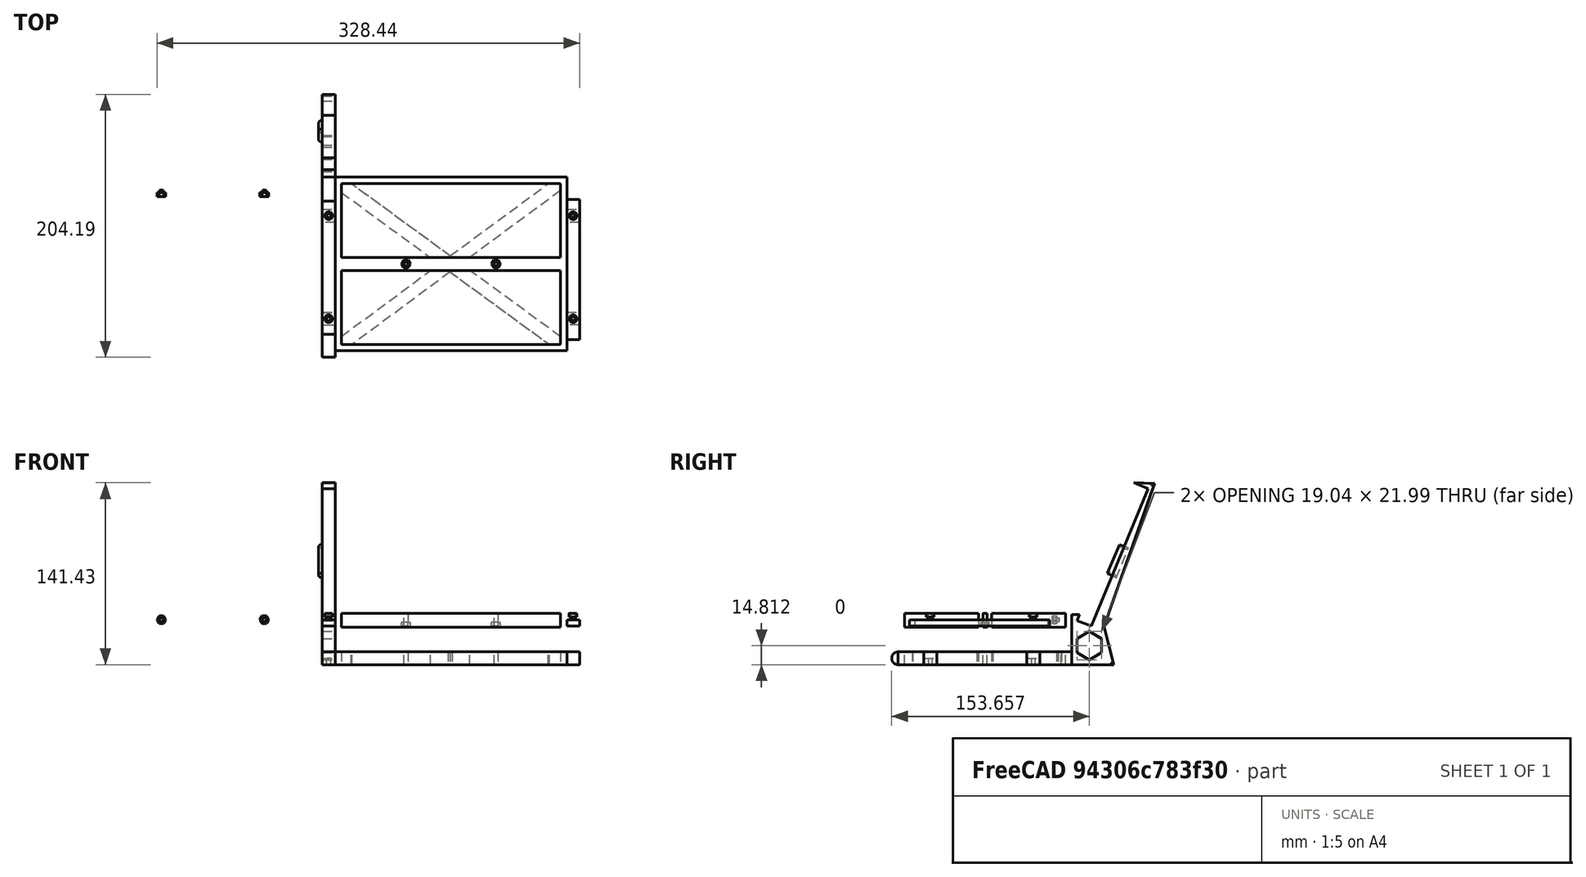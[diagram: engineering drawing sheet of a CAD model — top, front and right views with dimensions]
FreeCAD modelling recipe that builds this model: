
FCSTD DOCUMENT  (FreeCAD 0.16R6704 (Git))
Label: SOPORTE_BASE
License: All rights reserved
LicenseURL: http://en.wikipedia.org/wiki/All_rights_reserved
objects: Sketcher::SketchObject×13, PartDesign::Pocket×8, PartDesign::Pad×5, PartDesign::Fillet×3, Mesh::Feature×2
note: 42 computed .brp shape members not serialized (recipe doc carries the construction recipe); baked Part::Feature solids carry a one-line shape summary decoded from their .brp

FEATURE [Mesh::Feature] surround
  Placement = pos=(0,0,0) rot=(1,0,0;1.18682rad)
FEATURE [Sketcher::SketchObject] Sketch
  Placement = pos=(0,0,0) rot=(0.57735,0.57735,0.57735;2.0944rad)
  sketch-geometry (27):
    g0: LineSegment StartX=33.0856 StartY=111.432 StartZ=0 EndX=44.2008 EndY=106.79 EndZ=0
    g1: LineSegment StartX=44.2008 StartY=106.79 StartZ=0 EndX=0 EndY=0 EndZ=0
    g2: LineSegment StartX=-15 StartY=-20 StartZ=0 EndX=-40 EndY=-20 EndZ=0
    g3: LineSegment StartX=-150 StartY=-30 StartZ=0 EndX=17.4847 EndY=-30 EndZ=0
    g4: LineSegment StartX=17.4847 StartY=-30 StartZ=0 EndX=10 EndY=-0.272781 EndZ=0
    g5: LineSegment StartX=10 StartY=-0.272781 StartZ=0 EndX=49.1867 EndY=110.744 EndZ=0
    g6: LineSegment StartX=49.1867 StartY=110.744 StartZ=0 EndX=33.0856 EndY=111.432 EndZ=0
    g7: LineSegment StartX=0 StartY=0 StartZ=0 EndX=-10.9261 EndY=4.19036 EndZ=0
    g8: LineSegment StartX=-10.9261 StartY=4.19036 StartZ=0 EndX=-9.04306 EndY=8.84724 EndZ=0
    g9: LineSegment StartX=-9.04306 StartY=8.84724 StartZ=0 EndX=-15 EndY=8.84724 EndZ=0
    g10: LineSegment StartX=-15 StartY=8.84724 StartZ=0 EndX=-15 EndY=-20 EndZ=0
    g11: LineSegment StartX=8.17828 StartY=-20.6848 StartZ=0 EndX=8.17828 EndY=-9.6906 EndZ=0
    g12: LineSegment StartX=8.17828 StartY=-9.6906 StartZ=0 EndX=-1.34293 EndY=-4.19353 EndZ=0
    g13: LineSegment StartX=-1.34293 StartY=-4.19353 StartZ=0 EndX=-10.8641 EndY=-9.6906 EndZ=0
    g14: LineSegment StartX=-10.8641 StartY=-9.6906 StartZ=0 EndX=-10.8641 EndY=-20.6848 EndZ=0
    g15: LineSegment StartX=-10.8641 StartY=-20.6848 StartZ=0 EndX=-1.34293 EndY=-26.1818 EndZ=0
    g16: LineSegment StartX=-1.34293 StartY=-26.1818 StartZ=0 EndX=8.17828 EndY=-20.6848 EndZ=0
    g17: Circle [constr] CenterX=-1.34293 CenterY=-15.1877 CenterZ=0 NormalX=0 NormalY=0 NormalZ=1 Radius=10.9941
    g18: LineSegment StartX=-130 StartY=-20 StartZ=0 EndX=-130 EndY=-25 EndZ=0
    g19: LineSegment StartX=-130 StartY=-25 StartZ=0 EndX=-120 EndY=-25 EndZ=0
    g20: LineSegment StartX=-120 StartY=-25 StartZ=0 EndX=-120 EndY=-20 EndZ=0
    g21: LineSegment StartX=-130 StartY=-20 StartZ=0 EndX=-150 EndY=-20 EndZ=0
    g22: LineSegment StartX=-50 StartY=-20 StartZ=0 EndX=-50 EndY=-25 EndZ=0
    g23: LineSegment StartX=-50 StartY=-25 StartZ=0 EndX=-40 EndY=-25 EndZ=0
    g24: LineSegment StartX=-40 StartY=-25 StartZ=0 EndX=-40 EndY=-20 EndZ=0
    g25: LineSegment StartX=-50 StartY=-20 StartZ=0 EndX=-120 EndY=-20 EndZ=0
    g26: ArcOfCircle CenterX=-150 CenterY=-25 CenterZ=0 NormalX=0 NormalY=0 NormalZ=1 Radius=5 StartAngle=1.5708 EndAngle=4.71239
  constraints (57):
    c: Coincident(g0,g1)
    c: Coincident(g1,g-1)
    c: Horizontal(g2)
    c: Coincident(g3,g4)
    c: Coincident(g4,g5)
    c: Coincident(g5,g6)
    c: Coincident(g6,g0)
    c: Horizontal(g3)
    c: Coincident(g7,g8)
    c: Coincident(g8,g9)
    c: Coincident(g9,g10)
    c: Coincident(g-1,g7)
    c: Horizontal(g9)
    c: Coincident(g2,g10)
    c: DistanceY(g2,g-1) = 20
    c: DistanceY(g3,g-1) = 30
    c: DistanceX(g-1,g4) = 10
    c: Vertical(g10)
    c: DistanceX(g21,g2) = 135
    c: Coincident(g11,g12)
    c: Coincident(g12,g13)
    c: Coincident(g13,g14)
    c: Coincident(g14,g15)
    c: Coincident(g15,g16)
    c: Coincident(g16,g11)
    c: Equal(g11, g12-g16) x5
    c: PointOnObject(g11,g17)
    c: PointOnObject(g12,g17)
    c: PointOnObject(g13,g17)
    c: PointOnObject(g14,g17)
    c: PointOnObject(g15,g17)
    c: PointOnObject(g16,g17)
    c: Vertical(g14)
    c: DistanceX(g21,g-1) = 150
    c: Coincident(g18,g19)
    c: Horizontal(g19)
    c: Coincident(g19,g20)
    c: Vertical(g20)
    c: Vertical(g18)
    c: DistanceX(g19,g19) = 10
    c: Coincident(g25,g20)
    c: Coincident(g21,g18)
    c: Tangent(g2,g21)
    c: Coincident(g22,g23)
    c: Horizontal(g23)
    c: Coincident(g23,g24)
    c: Vertical(g24)
    c: Vertical(g22)
    c: DistanceX(g23,g23) = 10
    c: DistanceX(g19,g22) = 70
    c: Coincident(g2,g24)
    c: Coincident(g25,g22)
    c: Tangent(g2,g25)
    c: DistanceY(g24,g24) = 5
    c: DistanceY(g20,g20) = 5
    c: Tangent(g26,g21)
    c: Tangent(g3,g26)
FEATURE [PartDesign::Pad] Pad
  Length = 10
  Length2 = 100
  Placement = pos=(0,0,0) rot=(0.57735,0.57735,0.57735;2.0944rad)
  Sketch = -> Sketch
  Type = 0
FEATURE [Sketcher::SketchObject] Sketch001
  ExternalGeometry = -> [Pad]
  Placement = pos=(0,0,-25) rot=(0,0,-1;1.5708rad)
  Support = -> Pad [Face15]
  sketch-geometry (2):
    g0: Circle CenterX=45 CenterY=5 CenterZ=0 NormalX=0 NormalY=0 NormalZ=1 Radius=1.5
    g1: Circle CenterX=125 CenterY=5 CenterZ=0 NormalX=0 NormalY=0 NormalZ=1 Radius=1.5
  constraints (6):
    c: Radius(g0) = 1.5
    c: DistanceY(g-3,g0) = 5
    c: DistanceX(g-3,g0) = 5
    c: Radius(g1) = 1.5
    c: DistanceX(g1,g-4) = 5
    c: DistanceY(g-4,g1) = 5
FEATURE [PartDesign::Pocket] Pocket
  Length = 5
  Placement = pos=(0,0,0) rot=(0.57735,0.57735,0.57735;2.0944rad)
  Sketch = -> Sketch001
  Type = 0
FEATURE [Sketcher::SketchObject] Sketch003
  ExternalGeometry = -> [Pocket]
  Placement = pos=(0,0,0) rot=(0.57735,0.57735,-0.57735;4.18879rad)
  Support = -> Pocket [Face4]
  sketch-geometry (4):
    g0: LineSegment StartX=19.5719 StartY=-37.6948 StartZ=0 EndX=28.8724 EndY=-60.696 EndZ=0
    g1: LineSegment StartX=28.8724 StartY=-60.696 StartZ=0 EndX=22.072 EndY=-63.3961 EndZ=0
    g2: LineSegment StartX=22.072 StartY=-63.3961 StartZ=0 EndX=12.4716 EndY=-40.895 EndZ=0
    g3: LineSegment StartX=12.4716 StartY=-40.895 StartZ=0 EndX=19.5719 EndY=-37.6948 EndZ=0
  constraints (4):
    c: Coincident(g0,g1)
    c: Coincident(g1,g2)
    c: Coincident(g2,g3)
    c: Coincident(g3,g0)
FEATURE [PartDesign::Pad] Pad001
  Length = 3
  Length2 = 100
  Placement = pos=(0,0,0) rot=(0.57735,0.57735,0.57735;2.0944rad)
  Sketch = -> Sketch003
  Type = 0
FEATURE [PartDesign::Fillet] Fillet
  Base = -> Pad001 [Edge77,Edge73,Edge100,Edge80]
  Placement = pos=(0,0,0) rot=(0.57735,0.57735,0.57735;2.0944rad)
  Radius = 2
FEATURE [PartDesign::Fillet] Fillet001
  Base = -> Fillet [Edge62]
  Placement = pos=(0,0,0) rot=(0.57735,0.57735,0.57735;2.0944rad)
  Radius = 3
FEATURE [PartDesign::Fillet] Fillet002
  Base = -> Fillet001 [Edge37]
  Placement = pos=(0,0,0) rot=(0.57735,0.57735,0.57735;2.0944rad)
  Radius = 3
FEATURE [Sketcher::SketchObject] Sketch002
  Placement = pos=(0,0,-30) rot=(0.707107,0.707107,0;3.14159rad)
  Support = -> Fillet002 [Face5]
  sketch-geometry (14):
    g0: LineSegment StartX=-123.239 StartY=1.96418 StartZ=0 EndX=-121.507 EndY=4.96418 EndZ=0
    g1: LineSegment StartX=-121.507 StartY=4.96418 StartZ=0 EndX=-123.239 EndY=7.96418 EndZ=0
    g2: LineSegment StartX=-123.239 StartY=7.96418 StartZ=0 EndX=-126.704 EndY=7.96418 EndZ=0
    g3: LineSegment StartX=-126.704 StartY=7.96418 StartZ=0 EndX=-128.436 EndY=4.96418 EndZ=0
    g4: LineSegment StartX=-128.436 StartY=4.96418 StartZ=0 EndX=-126.704 EndY=1.96418 EndZ=0
    g5: LineSegment StartX=-126.704 StartY=1.96418 StartZ=0 EndX=-123.239 EndY=1.96418 EndZ=0
    g6: Circle [constr] CenterX=-124.971 CenterY=4.96418 CenterZ=0 NormalX=0 NormalY=0 NormalZ=1 Radius=3.4641
    g7: LineSegment StartX=-43.3346 StartY=7.98064 StartZ=0 EndX=-46.7987 EndY=7.98064 EndZ=0
    g8: LineSegment StartX=-46.7987 StartY=7.98064 StartZ=0 EndX=-48.5308 EndY=4.98064 EndZ=0
    g9: LineSegment StartX=-48.5308 StartY=4.98064 StartZ=0 EndX=-46.7987 EndY=1.98064 EndZ=0
    g10: LineSegment StartX=-46.7987 StartY=1.98064 StartZ=0 EndX=-43.3346 EndY=1.98064 EndZ=0
    g11: LineSegment StartX=-43.3346 StartY=1.98064 StartZ=0 EndX=-41.6026 EndY=4.98064 EndZ=0
    g12: LineSegment StartX=-41.6026 StartY=4.98064 StartZ=0 EndX=-43.3346 EndY=7.98064 EndZ=0
    g13: Circle [constr] CenterX=-45.0667 CenterY=4.98064 CenterZ=0 NormalX=0 NormalY=0 NormalZ=1 Radius=3.4641
  constraints (30):
    c: Coincident(g0,g1)
    c: Coincident(g1,g2)
    c: Coincident(g2,g3)
    c: Coincident(g3,g4)
    c: Coincident(g4,g5)
    c: Coincident(g5,g0)
    c: Equal(g0, g1-g5) x5
    c: PointOnObject(g0,g6)
    c: PointOnObject(g1,g6)
    c: PointOnObject(g2,g6)
    c: PointOnObject(g3,g6)
    c: PointOnObject(g4,g6)
    c: PointOnObject(g5,g6)
    c: Horizontal(g2)
    c: DistanceY(g0,g1) = 6
    c: Coincident(g7,g8)
    c: Coincident(g8,g9)
    c: Coincident(g9,g10)
    c: Coincident(g10,g11)
    c: Coincident(g11,g12)
    c: Coincident(g12,g7)
    c: Equal(g7, g8-g12) x5
    c: PointOnObject(g7,g13)
    c: PointOnObject(g8,g13)
    c: PointOnObject(g9,g13)
    c: PointOnObject(g10,g13)
    c: PointOnObject(g11,g13)
    c: PointOnObject(g12,g13)
    c: Horizontal(g7)
    c: DistanceY(g10,g7) = 6
FEATURE [PartDesign::Pocket] Pocket001
  Length = 3
  Placement = pos=(0,0,0) rot=(0.57735,0.57735,0.57735;2.0944rad)
  Sketch = -> Sketch002
  Type = 0
FEATURE [Mesh::Feature] SOPORTE_LATERAL_LADO
  Placement = pos=(192,0,0) rot=(0,0,1;0rad)
FEATURE [Sketcher::SketchObject] Sketch004
  Placement = pos=(0,0,-30) rot=(0,0,1;0rad)
  sketch-geometry (20):
    g0: LineSegment StartX=10 StartY=-50 StartZ=0 EndX=0 EndY=-50 EndZ=0
    g1: LineSegment StartX=0 StartY=-50 StartZ=0 EndX=0 EndY=-40 EndZ=0
    g2: LineSegment StartX=0 StartY=-40 StartZ=0 EndX=10 EndY=-40 EndZ=0
    g3: LineSegment StartX=10 StartY=-40 StartZ=0 EndX=10 EndY=-15 EndZ=0
    g4: LineSegment StartX=10 StartY=-15 StartZ=0 EndX=190 EndY=-15 EndZ=0
    g5: LineSegment StartX=190 StartY=-15 StartZ=0 EndX=190 EndY=-40 EndZ=0
    g6: LineSegment StartX=190 StartY=-40 StartZ=0 EndX=200 EndY=-40 EndZ=0
    g7: LineSegment StartX=200 StartY=-40 StartZ=0 EndX=200 EndY=-50 EndZ=0
    g8: LineSegment StartX=200 StartY=-50 StartZ=0 EndX=190 EndY=-50 EndZ=0
    g9: LineSegment StartX=190 StartY=-50 StartZ=0 EndX=190 EndY=-120 EndZ=0
    g10: LineSegment StartX=190 StartY=-120 StartZ=0 EndX=200 EndY=-120 EndZ=0
    g11: LineSegment StartX=200 StartY=-120 StartZ=0 EndX=200 EndY=-130 EndZ=0
    g12: LineSegment StartX=200 StartY=-130 StartZ=0 EndX=190 EndY=-130 EndZ=0
    g13: LineSegment StartX=190 StartY=-130 StartZ=0 EndX=190 EndY=-150 EndZ=0
    g14: LineSegment StartX=190 StartY=-150 StartZ=0 EndX=10 EndY=-150 EndZ=0
    g15: LineSegment StartX=10 StartY=-150 StartZ=0 EndX=10 EndY=-130.022 EndZ=0
    g16: LineSegment StartX=10 StartY=-130.022 StartZ=0 EndX=0 EndY=-130.022 EndZ=0
    g17: LineSegment StartX=0 StartY=-130.022 StartZ=0 EndX=0 EndY=-120.229 EndZ=0
    g18: LineSegment StartX=0 StartY=-120.229 StartZ=0 EndX=10 EndY=-120.229 EndZ=0
    g19: LineSegment StartX=10 StartY=-120.229 StartZ=0 EndX=10 EndY=-50 EndZ=0
  constraints (58):
    c: PointOnObject(g0,g-2)
    c: Coincident(g0,g1)
    c: PointOnObject(g1,g-2)
    c: Coincident(g1,g2)
    c: Coincident(g2,g3)
    c: Vertical(g3)
    c: Coincident(g3,g4)
    c: Horizontal(g4)
    c: Coincident(g4,g5)
    c: Coincident(g5,g6)
    c: Coincident(g6,g7)
    c: Vertical(g7)
    c: Coincident(g7,g8)
    c: Horizontal(g8)
    c: Coincident(g8,g9)
    c: Vertical(g9)
    c: Coincident(g9,g10)
    c: Coincident(g10,g11)
    c: Coincident(g11,g12)
    c: Horizontal(g12)
    c: Coincident(g12,g13)
    c: Vertical(g13)
    c: Coincident(g13,g14)
    c: Horizontal(g14)
    c: Coincident(g14,g15)
    c: Coincident(g15,g16)
    c: PointOnObject(g16,g-2)
    c: Coincident(g16,g17)
    c: PointOnObject(g17,g-2)
    c: Coincident(g17,g18)
    c: Horizontal(g18)
    c: Coincident(g18,g19)
    c: Vertical(g19)
    c: Coincident(g0,g19)
    c: Horizontal(g2)
    c: Horizontal(g0)
    c: Horizontal(g16)
    c: Vertical(g15)
    c: Vertical(g11)
    c: Horizontal(g10)
    c: DistanceY(g14,g3) = 135
    c: DistanceX(g16,g11) = 200
    c: DistanceX(g4,g4) = 180
    c: DistanceX(g-1,g3) = 10
    c: DistanceX(g-1,g14) = 10
    c: DistanceX(g14,g14) = 180
    c: DistanceX(g-1,g18) = 10
    c: DistanceX(g0,g8) = 180
    c: Horizontal(g6)
    c: Vertical(g5)
    c: DistanceY(g7,g7) = 10
    c: DistanceY(g11,g11) = 10
    c: DistanceX(g6,g6) = 10
    c: DistanceY(g1,g-1) = 40
    c: DistanceY(g1,g1) = 10
    c: DistanceY(g3,g-1) = 15
    c: DistanceY(g5,g4) = 25
    c: DistanceY(g10,g7) = 70
FEATURE [PartDesign::Pad] Pad002
  Length = 10
  Length2 = 100
  Placement = pos=(0,0,-30) rot=(0,0,1;0rad)
  Sketch = -> Sketch004
  Type = 0
FEATURE [Sketcher::SketchObject] Sketch005
  ExternalGeometry = -> [Pad002]
  Placement = pos=(0,0,-20) rot=(0,0,1;0rad)
  Support = -> Pad002 [Face22]
  sketch-geometry (10):
    g0: Circle CenterX=65 CenterY=-82.5 CenterZ=0 NormalX=0 NormalY=0 NormalZ=1 Radius=1.5
    g1: Circle CenterX=135 CenterY=-82.5 CenterZ=0 NormalX=0 NormalY=0 NormalZ=1 Radius=1.5
    g2: LineSegment StartX=15 StartY=-20 StartZ=0 EndX=185 EndY=-20 EndZ=0
    g3: LineSegment StartX=185 StartY=-20 StartZ=0 EndX=185 EndY=-77.5 EndZ=0
    g4: LineSegment StartX=185 StartY=-77.5 StartZ=0 EndX=15 EndY=-77.5 EndZ=0
    g5: LineSegment StartX=15 StartY=-77.5 StartZ=0 EndX=15 EndY=-20 EndZ=0
    g6: LineSegment StartX=15 StartY=-87.5 StartZ=0 EndX=185 EndY=-87.5 EndZ=0
    g7: LineSegment StartX=185 StartY=-87.5 StartZ=0 EndX=185 EndY=-145 EndZ=0
    g8: LineSegment StartX=185 StartY=-145 StartZ=0 EndX=15 EndY=-145 EndZ=0
    g9: LineSegment StartX=15 StartY=-145 StartZ=0 EndX=15 EndY=-87.5 EndZ=0
  constraints (30):
    c: Radius(g1) = 1.5
    c: Radius(g0) = 1.5
    c: DistanceY(g0,g-3) = 67.5
    c: DistanceY(g1,g-3) = 67.5
    c: DistanceX(g0,g1) = 70
    c: DistanceX(g1,g-5) = 65
    c: Coincident(g2,g3)
    c: Coincident(g3,g4)
    c: Coincident(g4,g5)
    c: Coincident(g5,g2)
    c: Horizontal(g2)
    c: Horizontal(g4)
    c: Vertical(g3)
    c: Vertical(g5)
    c: Coincident(g6,g7)
    c: Coincident(g7,g8)
    c: Coincident(g8,g9)
    c: Coincident(g9,g6)
    c: Horizontal(g6)
    c: Horizontal(g8)
    c: Vertical(g7)
    c: Vertical(g9)
    c: DistanceY(g2,g-3) = 5
    c: DistanceX(g-3,g2) = 5
    c: DistanceX(g-4,g8) = 5
    c: DistanceY(g-4,g8) = 5
    c: DistanceX(g7,g-4) = 5
    c: DistanceX(g2,g-3) = 5
    c: DistanceY(g6,g4) = 10
    c: DistanceY(g0,g4) = 5
FEATURE [PartDesign::Pocket] Pocket002
  Length = 11
  Placement = pos=(0,0,-30) rot=(0,0,1;0rad)
  Sketch = -> Sketch005
  Type = 0
FEATURE [Sketcher::SketchObject] Sketch006
  ExternalGeometry = -> [Pocket002]
  Placement = pos=(0,0,-20) rot=(0,0,1;0rad)
  Support = -> Pocket002 [Face5]
  sketch-geometry (4):
    g0: LineSegment StartX=15.5445 StartY=-15 StartZ=0 EndX=9.9428 EndY=-23.2838 EndZ=0
    g1: LineSegment StartX=9.9428 StartY=-23.2838 StartZ=0 EndX=183.213 EndY=-150 EndZ=0
    g2: LineSegment StartX=183.213 StartY=-150 StartZ=0 EndX=189.107 EndY=-141.922 EndZ=0
    g3: LineSegment StartX=189.107 StartY=-141.922 StartZ=0 EndX=15.5445 EndY=-15 EndZ=0
  constraints (8):
    c: Coincident(g0,g1)
    c: PointOnObject(g1,g-4)
    c: Coincident(g1,g2)
    c: Coincident(g2,g3)
    c: Coincident(g0,g3)
    c: PointOnObject(g0,g-3)
    c: Distance(g0,g0) = 10
    c: Distance(g1,g2) = 10
FEATURE [PartDesign::Pad] Pad003
  Length = 10
  Length2 = 100
  Placement = pos=(0,0,-30) rot=(0,0,1;0rad)
  Reversed = true
  Sketch = -> Sketch006
  Type = 0
FEATURE [Sketcher::SketchObject] Sketch007
  ExternalGeometry = -> [Pad003]
  Placement = pos=(0,0,-20) rot=(0,0,1;0rad)
  Support = -> Pad003 [Face5]
  sketch-geometry (4):
    g0: LineSegment StartX=16.4452 StartY=-150 StartZ=0 EndX=10.8233 EndY=-141.73 EndZ=0
    g1: LineSegment StartX=10.8233 StartY=-141.73 StartZ=0 EndX=182.344 EndY=-15 EndZ=0
    g2: LineSegment StartX=182.344 StartY=-15 StartZ=0 EndX=188.253 EndY=-23.0677 EndZ=0
    g3: LineSegment StartX=188.253 StartY=-23.0677 StartZ=0 EndX=16.4452 EndY=-150 EndZ=0
  constraints (8):
    c: PointOnObject(g0,g-3)
    c: Coincident(g0,g1)
    c: PointOnObject(g1,g-4)
    c: Coincident(g1,g2)
    c: Coincident(g2,g3)
    c: Coincident(g3,g0)
    c: Distance(g0) = 10
    c: Distance(g2) = 10
FEATURE [PartDesign::Pad] Pad004
  Length = 10
  Length2 = 100
  Placement = pos=(0,0,-30) rot=(0,0,1;0rad)
  Reversed = true
  Sketch = -> Sketch007
  Type = 0
FEATURE [Sketcher::SketchObject] Sketch008
  Placement = pos=(0,0,-30) rot=(1,0,0;3.14159rad)
  Support = -> Pad004 [Face68]
  sketch-geometry (14):
    g0: LineSegment StartX=66.725 StartY=85.5166 StartZ=0 EndX=63.2609 EndY=85.5166 EndZ=0
    g1: LineSegment StartX=63.2609 StartY=85.5166 StartZ=0 EndX=61.5289 EndY=82.5166 EndZ=0
    g2: LineSegment StartX=61.5289 StartY=82.5166 StartZ=0 EndX=63.2609 EndY=79.5166 EndZ=0
    g3: LineSegment StartX=63.2609 StartY=79.5166 StartZ=0 EndX=66.725 EndY=79.5166 EndZ=0
    g4: LineSegment StartX=66.725 StartY=79.5166 StartZ=0 EndX=68.4571 EndY=82.5166 EndZ=0
    g5: LineSegment StartX=68.4571 StartY=82.5166 StartZ=0 EndX=66.725 EndY=85.5166 EndZ=0
    g6: Circle [constr] CenterX=64.993 CenterY=82.5166 CenterZ=0 NormalX=0 NormalY=0 NormalZ=1 Radius=3.4641
    g7: LineSegment StartX=136.743 StartY=85.4232 StartZ=0 EndX=133.279 EndY=85.4232 EndZ=0
    g8: LineSegment StartX=133.279 StartY=85.4232 StartZ=0 EndX=131.547 EndY=82.4232 EndZ=0
    g9: LineSegment StartX=131.547 StartY=82.4232 StartZ=0 EndX=133.279 EndY=79.4232 EndZ=0
    g10: LineSegment StartX=133.279 StartY=79.4232 StartZ=0 EndX=136.743 EndY=79.4232 EndZ=0
    g11: LineSegment StartX=136.743 StartY=79.4232 StartZ=0 EndX=138.475 EndY=82.4232 EndZ=0
    g12: LineSegment StartX=138.475 StartY=82.4232 StartZ=0 EndX=136.743 EndY=85.4232 EndZ=0
    g13: Circle [constr] CenterX=135.011 CenterY=82.4232 CenterZ=0 NormalX=0 NormalY=0 NormalZ=1 Radius=3.4641
  constraints (30):
    c: Coincident(g0,g1)
    c: Coincident(g1,g2)
    c: Coincident(g2,g3)
    c: Coincident(g3,g4)
    c: Coincident(g4,g5)
    c: Coincident(g5,g0)
    c: Equal(g0, g1-g5) x5
    c: PointOnObject(g0,g6)
    c: PointOnObject(g1,g6)
    c: PointOnObject(g2,g6)
    c: PointOnObject(g3,g6)
    c: PointOnObject(g4,g6)
    c: PointOnObject(g5,g6)
    c: Coincident(g7,g8)
    c: Coincident(g8,g9)
    c: Coincident(g9,g10)
    c: Coincident(g10,g11)
    c: Coincident(g11,g12)
    c: Coincident(g12,g7)
    c: Equal(g7, g8-g12) x5
    c: PointOnObject(g7,g13)
    c: PointOnObject(g8,g13)
    c: PointOnObject(g9,g13)
    c: PointOnObject(g10,g13)
    c: PointOnObject(g11,g13)
    c: PointOnObject(g12,g13)
    c: Horizontal(g10)
    c: Horizontal(g3)
    c: DistanceY(g3,g0) = 6
    c: DistanceY(g10,g7) = 6
FEATURE [PartDesign::Pocket] Pocket003
  Length = 3
  Placement = pos=(0,0,-30) rot=(0,0,1;0rad)
  Sketch = -> Sketch008
  Type = 0
FEATURE [Sketcher::SketchObject] Sketch009
  Placement = pos=(0,0,-30) rot=(0.57735,-0.57735,-0.57735;2.0944rad)
  Support = -> Pocket003 [Face8]
  sketch-geometry (4):
    g0: LineSegment StartX=33.4989 StartY=5 StartZ=0 EndX=137.212 EndY=5 EndZ=0
    g1: LineSegment StartX=137.212 StartY=5 StartZ=0 EndX=137.212 EndY=0 EndZ=0
    g2: LineSegment StartX=137.212 StartY=0 StartZ=0 EndX=33.4989 EndY=0 EndZ=0
    g3: LineSegment StartX=33.4989 StartY=0 StartZ=0 EndX=33.4989 EndY=5 EndZ=0
  constraints (10):
    c: Coincident(g0,g1)
    c: Coincident(g1,g2)
    c: Coincident(g2,g3)
    c: Coincident(g3,g0)
    c: Horizontal(g0)
    c: Horizontal(g2)
    c: Vertical(g1)
    c: Vertical(g3)
    c: PointOnObject(g1,g-1)
    c: DistanceY(g3,g3) = 5
FEATURE [PartDesign::Pocket] Pocket004
  Length = 10
  Placement = pos=(0,0,-30) rot=(0,0,1;0rad)
  Sketch = -> Sketch009
  Type = 0
FEATURE [Sketcher::SketchObject] Sketch010
  Placement = pos=(200,0,-30) rot=(0.57735,0.57735,0.57735;2.0944rad)
  Support = -> Pocket004 [Face91]
  sketch-geometry (4):
    g0: LineSegment StartX=-141.342 StartY=5 StartZ=0 EndX=-32.3049 EndY=5 EndZ=0
    g1: LineSegment StartX=-32.3049 StartY=5 StartZ=0 EndX=-32.3049 EndY=0 EndZ=0
    g2: LineSegment StartX=-32.3049 StartY=0 StartZ=0 EndX=-141.342 EndY=0 EndZ=0
    g3: LineSegment StartX=-141.342 StartY=0 StartZ=0 EndX=-141.342 EndY=5 EndZ=0
  constraints (10):
    c: Coincident(g0,g1)
    c: Coincident(g1,g2)
    c: Coincident(g2,g3)
    c: Coincident(g3,g0)
    c: Horizontal(g0)
    c: Horizontal(g2)
    c: Vertical(g1)
    c: Vertical(g3)
    c: PointOnObject(g1,g-1)
    c: DistanceY(g3,g3) = 5
FEATURE [PartDesign::Pocket] Pocket005
  Length = 10
  Placement = pos=(0,0,-30) rot=(0,0,1;0rad)
  Sketch = -> Sketch010
  Type = 0
FEATURE [Sketcher::SketchObject] Sketch011
  Placement = pos=(0,0,-20) rot=(0,0,1;0rad)
  Support = -> Pocket005 [Face76]
  sketch-geometry (4):
    g0: Circle CenterX=5.03607 CenterY=-44.9743 CenterZ=0 NormalX=0 NormalY=0 NormalZ=1 Radius=1.5
    g1: Circle CenterX=4.9817 CenterY=-125.071 CenterZ=0 NormalX=0 NormalY=0 NormalZ=1 Radius=1.5
    g2: Circle CenterX=194.833 CenterY=-45.0217 CenterZ=0 NormalX=0 NormalY=0 NormalZ=1 Radius=1.5
    g3: Circle CenterX=194.878 CenterY=-125.01 CenterZ=0 NormalX=0 NormalY=0 NormalZ=1 Radius=1.5
  constraints (4):
    c: Radius(g0) = 1.5
    c: Radius(g1) = 1.5
    c: Radius(g2) = 1.5
    c: Radius(g3) = 1.5
FEATURE [PartDesign::Pocket] Pocket006
  Length = 5
  Placement = pos=(0,0,-30) rot=(0,0,1;0rad)
  Sketch = -> Sketch011
  Type = 0
FEATURE [Sketcher::SketchObject] Sketch012
  Placement = pos=(0,0,-20) rot=(0,0,1;0rad)
  Support = -> Pocket006 [Face4]
  sketch-geometry (4):
    g0: Circle CenterX=5.01646 CenterY=-44.9718 CenterZ=0 NormalX=0 NormalY=0 NormalZ=1 Radius=3
    g1: Circle CenterX=4.97234 CenterY=-125.069 CenterZ=0 NormalX=0 NormalY=0 NormalZ=1 Radius=3
    g2: Circle CenterX=194.878 CenterY=-125.061 CenterZ=0 NormalX=0 NormalY=0 NormalZ=1 Radius=3
    g3: Circle CenterX=194.863 CenterY=-45.0158 CenterZ=0 NormalX=0 NormalY=0 NormalZ=1 Radius=3
  constraints (4):
    c: Radius(g0) = 3
    c: Radius(g1) = 3
    c: Radius(g2) = 3
    c: Radius(g3) = 3
FEATURE [PartDesign::Pocket] Pocket007
  Length = 3
  Placement = pos=(0,0,-30) rot=(0,0,1;0rad)
  Sketch = -> Sketch012
  Type = 0
